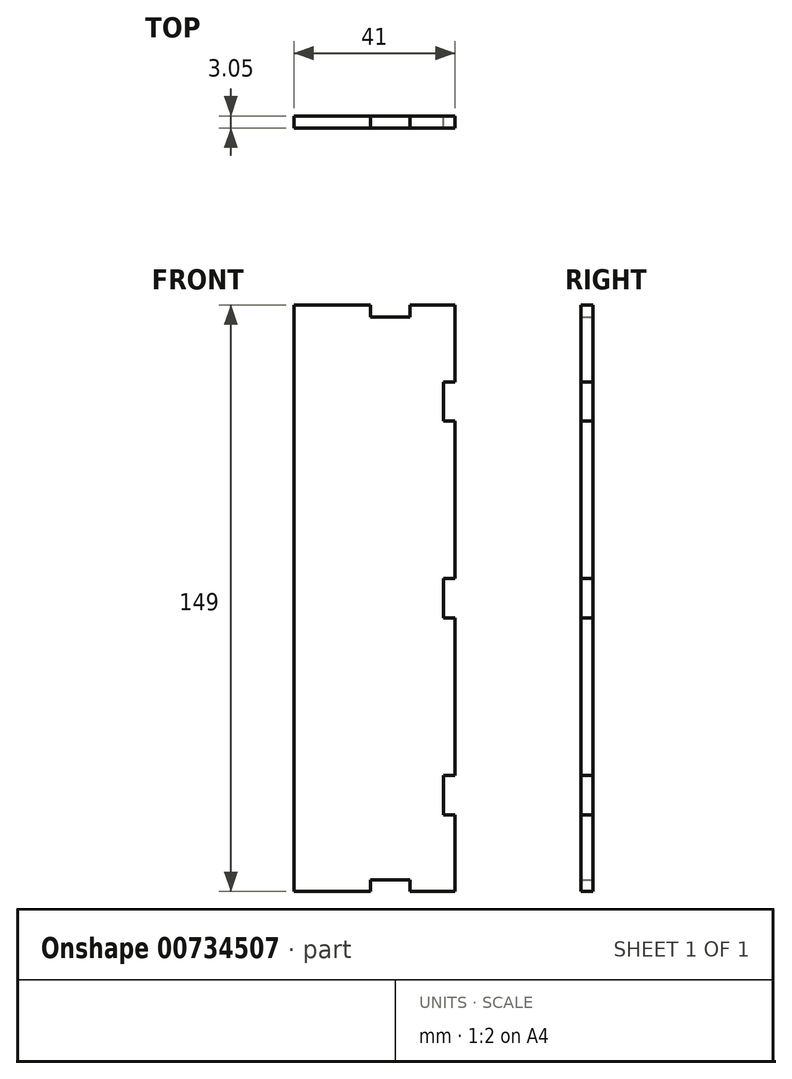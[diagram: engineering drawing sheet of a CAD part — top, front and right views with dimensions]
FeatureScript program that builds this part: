
annotation { "Feature Type Name" : "Feature", "Feature Type Description" : "" }
export const myFeature = defineFeature(function(context is Context, id is Id, definition is map)
    precondition{}
    {
        {
            var Q0;
            Q0=qCreatedBy(makeId("Front.planeOp"),FACE);
            var sketch = newSketch(context, id + "F0", { "sketchPlane" : qUnion([Q0])});
            skLineSegment(sketch, "E0", {"start": v(9, -74.5) * mm, "end": v(9, -71.5) * mm});
            skLineSegment(sketch, "E1", {"start": v(9, -71.5) * mm, "end": v(-1, -71.5) * mm});
            skLineSegment(sketch, "E2", {"start": v(-1, -71.5) * mm, "end": v(-1, -74.5) * mm});
            skLineSegment(sketch, "E3", {"start": v(-1, -74.5) * mm, "end": v(-20.5, -74.5) * mm});
            skLineSegment(sketch, "E4", {"start": v(-20.5, -74.5) * mm, "end": v(-20.5, 74.5) * mm});
            skLineSegment(sketch, "E5", {"start": v(-20.5, 74.5) * mm, "end": v(-1, 74.5) * mm});
            skLineSegment(sketch, "E6", {"start": v(-1, 74.5) * mm, "end": v(-1, 71.5) * mm});
            skLineSegment(sketch, "E7", {"start": v(-1, 71.5) * mm, "end": v(9, 71.5) * mm});
            skLineSegment(sketch, "E8", {"start": v(9, 71.5) * mm, "end": v(9, 74.5) * mm});
            skLineSegment(sketch, "E9", {"start": v(9, 74.5) * mm, "end": v(20.5, 74.5) * mm});
            skLineSegment(sketch, "E10", {"start": v(20.5, 74.5) * mm, "end": v(20.5, 55) * mm});
            skLineSegment(sketch, "E11", {"start": v(20.5, 55) * mm, "end": v(17.5, 55) * mm});
            skLineSegment(sketch, "E12", {"start": v(17.5, 55) * mm, "end": v(17.5, 45) * mm});
            skLineSegment(sketch, "E13", {"start": v(17.5, 45) * mm, "end": v(20.5, 45) * mm});
            skLineSegment(sketch, "E14", {"start": v(20.5, 45) * mm, "end": v(20.5, 5) * mm});
            skLineSegment(sketch, "E15", {"start": v(20.5, 5) * mm, "end": v(17.5, 5) * mm});
            skLineSegment(sketch, "E16", {"start": v(17.5, 5) * mm, "end": v(17.5, -5) * mm});
            skLineSegment(sketch, "E17", {"start": v(17.5, -5) * mm, "end": v(20.5, -5) * mm});
            skLineSegment(sketch, "E18", {"start": v(20.5, -5) * mm, "end": v(20.5, -45) * mm});
            skLineSegment(sketch, "E19", {"start": v(20.5, -45) * mm, "end": v(17.5, -45) * mm});
            skLineSegment(sketch, "E20", {"start": v(17.5, -45) * mm, "end": v(17.5, -55) * mm});
            skLineSegment(sketch, "E21", {"start": v(17.5, -55) * mm, "end": v(20.5, -55) * mm});
            skLineSegment(sketch, "E22", {"start": v(20.5, -55) * mm, "end": v(20.5, -74.5) * mm});
            skLineSegment(sketch, "E23", {"start": v(20.5, -74.5) * mm, "end": v(9, -74.5) * mm});
            skSolve(sketch);
        }
        {
            var Q0;
            Q0 = qSketchRegion(id + "F0", true);
            extrude(context, id + "F1", {"entities" : qUnion([Q0]), "depth" : 3.05 * mm, "offsetDistance" : 25.4 * mm});
        }
    });
